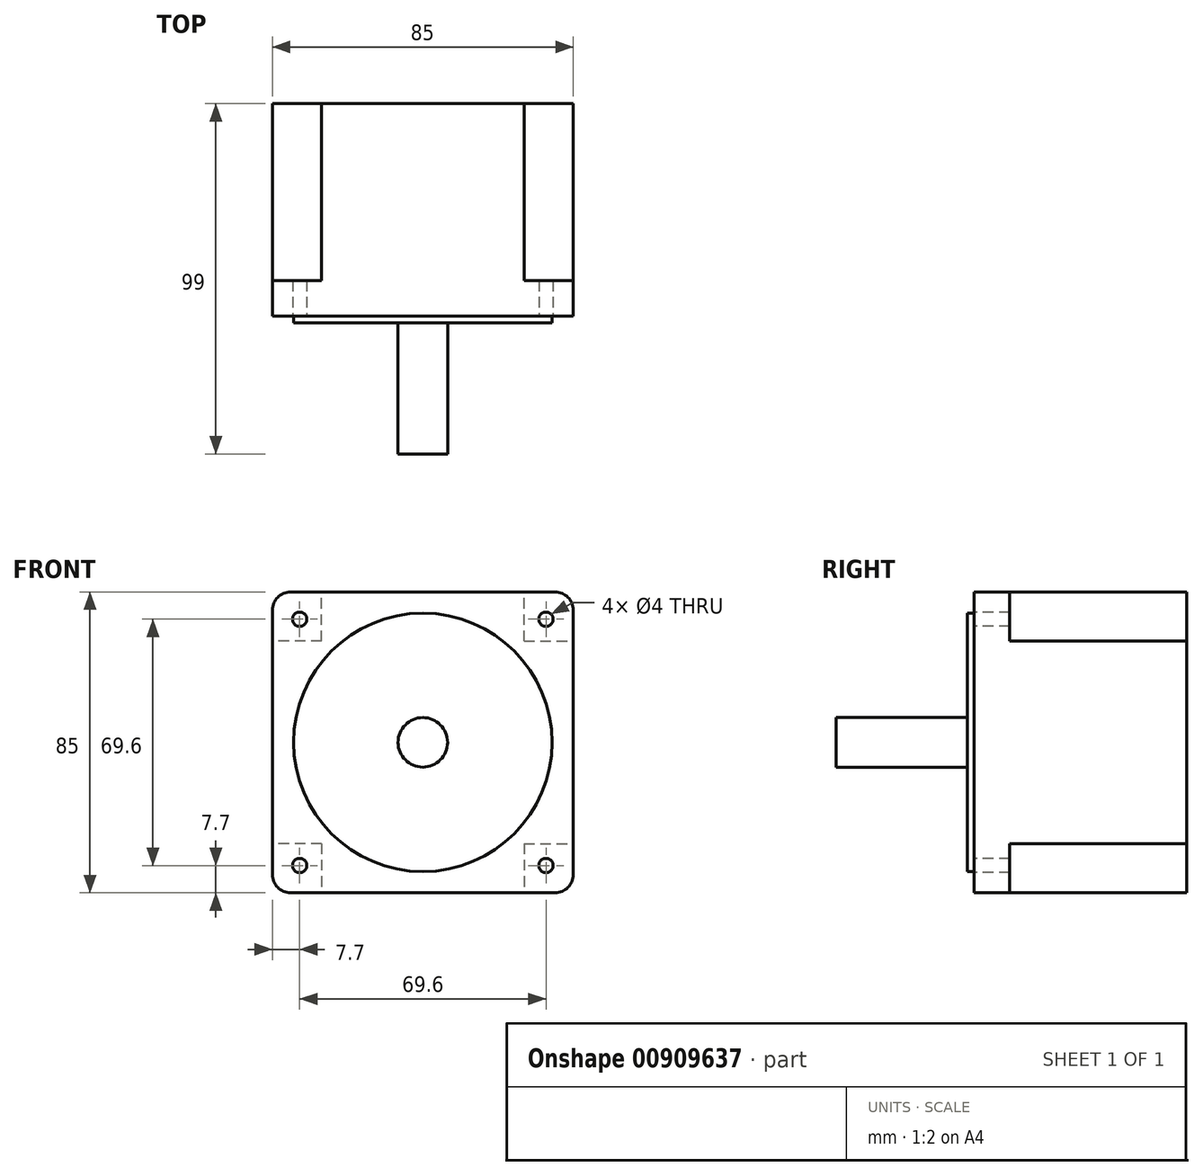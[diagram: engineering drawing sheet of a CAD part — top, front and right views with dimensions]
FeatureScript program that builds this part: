
annotation { "Feature Type Name" : "Feature", "Feature Type Description" : "" }
export const myFeature = defineFeature(function(context is Context, id is Id, definition is map)
    precondition{}
    {
        {
            var Q0;
            Q0=qCreatedBy(makeId("Front.planeOp"),FACE);
            var sketch = newSketch(context, id + "F0", { "sketchPlane" : qUnion([Q0])});
            skLineSegment(sketch, "E0.bottom", {"start": v(42.5, 42.5) * mm, "end": v(-42.5, 42.5) * mm});
            skLineSegment(sketch, "E0.top", {"start": v(42.5, -42.5) * mm, "end": v(-42.5, -42.5) * mm});
            skLineSegment(sketch, "E0.left", {"start": v(42.5, 42.5) * mm, "end": v(42.5, -42.5) * mm});
            skLineSegment(sketch, "E0.right", {"start": v(-42.5, 42.5) * mm, "end": v(-42.5, -42.5) * mm});
            skPoint(sketch, "E0.middle", {"position": v(0, 0) * mm});
            skSolve(sketch);
        }
        {
            var Q0;
            Q0 = qSketchRegion(id + "F0", true);
            extrude(context, id + "F1", {"entities" : qUnion([Q0]), "depth" : 10 * mm, "offsetDistance" : 25.4 * mm});
        }
        {
            var Q0;
            Q0=makeQuery(id+"F1.opExtrude","SWEPT_EDGE",EDGE,{"disambiguationData":[OSD([sQuery(id+"F0.wireOp",EDGE,"E0.top"),sQuery(id+"F0.wireOp",EDGE,"E0.left")])]});
            var Q1;
            Q1=makeQuery(id+"F1.opExtrude","SWEPT_EDGE",EDGE,{"disambiguationData":[OSD([sQuery(id+"F0.wireOp",EDGE,"E0.bottom"),sQuery(id+"F0.wireOp",EDGE,"E0.left")])]});
            var Q2;
            Q2=makeQuery(id+"F1.opExtrude","SWEPT_EDGE",EDGE,{"disambiguationData":[OSD([sQuery(id+"F0.wireOp",EDGE,"E0.bottom"),sQuery(id+"F0.wireOp",EDGE,"E0.right")])]});
            var Q3;
            Q3=makeQuery(id+"F1.opExtrude","SWEPT_EDGE",EDGE,{"disambiguationData":[OSD([sQuery(id+"F0.wireOp",EDGE,"E0.top"),sQuery(id+"F0.wireOp",EDGE,"E0.right")])]});
            fillet(context, id + "F2", {"entities" : qUnion([Q0, Q1, Q2, Q3]), "radius" : 5.08 * mm, "tangentPropagation" : true, "allowEdgeOverflow" : false});
        }
        {
            var Q0;
            Q0=makeQuery(id+"F1.opExtrude","CAP_FACE",FACE,{"disambiguationData":[OSD([sQuery(id+"F0.wireOp",EDGE,"E0.bottom"),sQuery(id+"F0.wireOp",EDGE,"E0.top"),sQuery(id+"F0.wireOp",EDGE,"E0.left"),sQuery(id+"F0.wireOp",EDGE,"E0.right")])],"isStart":false});
            var sketch = newSketch(context, id + "F3", { "sketchPlane" : qUnion([Q0])});
            skPoint(sketch, "E1.middle", {"position": v(0, 0) * mm});
            skCircle(sketch, "E2", {"center": v(-34.8, 34.8) * mm, "radius": 2 * mm});
            skCircle(sketch, "E3", {"center": v(34.8, 34.8) * mm, "radius": 2 * mm});
            skCircle(sketch, "E4", {"center": v(34.8, -34.8) * mm, "radius": 2 * mm});
            skCircle(sketch, "E5", {"center": v(-34.8, -34.8) * mm, "radius": 2 * mm});
            skCircle(sketch, "E6", {"center": v(0, 0) * mm, "radius": 36.51 * mm});
            skSolve(sketch);
        }
        {
            var Q0;
            Q0=makeQuery(id+"F3.imprint","IMPRINT",FACE,{"disambiguationData":[TD([[makeQuery(id+"F3.imprint","IMPRINT",EDGE,{"derivedFrom":sQuery(id+"F3.wireOp",EDGE,"E2")}),1.0]])]});
            var Q1;
            Q1=makeQuery(id+"F3.imprint","IMPRINT",FACE,{"disambiguationData":[TD([[makeQuery(id+"F3.imprint","IMPRINT",EDGE,{"derivedFrom":sQuery(id+"F3.wireOp",EDGE,"E3")}),1.0]])]});
            var Q2;
            Q2=makeQuery(id+"F3.imprint","IMPRINT",FACE,{"disambiguationData":[TD([[makeQuery(id+"F3.imprint","IMPRINT",EDGE,{"derivedFrom":sQuery(id+"F3.wireOp",EDGE,"E4")}),1.0]])]});
            var Q3;
            Q3=makeQuery(id+"F3.imprint","IMPRINT",FACE,{"disambiguationData":[TD([[makeQuery(id+"F3.imprint","IMPRINT",EDGE,{"derivedFrom":sQuery(id+"F3.wireOp",EDGE,"E5")}),1.0]])]});
            extrude(context, id + "F4", {"entities" : qUnion([Q0, Q1, Q2, Q3]), "operationType" : NewBodyOperationType.REMOVE, "oppositeDirection" : true, "depth" : 25.4 * mm, "offsetDistance" : 25.4 * mm});
        }
        {
            var Q0;
            Q0=makeQuery(id+"F3.imprint","IMPRINT",FACE,{"disambiguationData":[TD([[makeQuery(id+"F3.imprint","IMPRINT",EDGE,{"derivedFrom":sQuery(id+"F3.wireOp",EDGE,"E6")}),1.0]])]});
            extrude(context, id + "F5", {"entities" : qUnion([Q0]), "operationType" : NewBodyOperationType.ADD, "depth" : 2 * mm, "offsetDistance" : 25.4 * mm});
        }
        {
            var Q0;
            Q0=makeQuery(id+"F5.opExtrude","CAP_FACE",FACE,{"disambiguationData":[OSD([sQuery(id+"F3.wireOp",EDGE,"E6")])],"isStart":false});
            var sketch = newSketch(context, id + "F6", { "sketchPlane" : qUnion([Q0])});
            skCircle(sketch, "E7", {"center": v(0, 0) * mm, "radius": 7 * mm});
            skSolve(sketch);
        }
        {
            var Q0;
            Q0 = qSketchRegion(id + "F6", true);
            extrude(context, id + "F7", {"entities" : qUnion([Q0]), "operationType" : NewBodyOperationType.ADD, "depth" : 37 * mm, "offsetDistance" : 25.4 * mm});
        }
        {
            var Q0;
            Q0=makeQuery(id+"F1.opExtrude","CAP_FACE",FACE,{"disambiguationData":[OSD([sQuery(id+"F0.wireOp",EDGE,"E0.bottom"),sQuery(id+"F0.wireOp",EDGE,"E0.top"),sQuery(id+"F0.wireOp",EDGE,"E0.left"),sQuery(id+"F0.wireOp",EDGE,"E0.right")])],"isStart":true});
            var sketch = newSketch(context, id + "F8", { "sketchPlane" : qUnion([Q0])});
            skLineSegment(sketch, "E8", {"start": v(34.8, 34.8) * mm, "end": v(41.01, 41.01) * mm, "construction": true});
            skLineSegment(sketch, "E9", {"start": v(41.01, 41.01) * mm, "end": v(28.58, 28.58) * mm, "construction": true});
            skLineSegment(sketch, "E10.bottom", {"start": v(28.58, 28.58) * mm, "end": v(-28.58, 28.58) * mm});
            skLineSegment(sketch, "E10.left", {"start": v(28.58, 28.58) * mm, "end": v(28.58, -28.58) * mm});
            skLineSegment(sketch, "E10.right", {"start": v(-28.58, 28.58) * mm, "end": v(-28.58, -28.58) * mm});
            skPoint(sketch, "E10.middle", {"position": v(0, 0) * mm});
            skLineSegment(sketch, "E11", {"start": v(-28.58, 28.58) * mm, "end": v(-28.58, 42.5) * mm, "construction": true});
            skLineSegment(sketch, "E12", {"start": v(-28.58, -28.58) * mm, "end": v(-42.5, -28.58) * mm, "construction": true});
            skLineSegment(sketch, "E13", {"start": v(-28.58, -28.58) * mm, "end": v(-28.58, -42.5) * mm, "construction": true});
            skLineSegment(sketch, "E14", {"start": v(28.58, -28.58) * mm, "end": v(42.5, -28.58) * mm, "construction": true});
            skLineSegment(sketch, "E15.top", {"start": v(28.58, 42.5) * mm, "end": v(-28.58, 42.5) * mm});
            skLineSegment(sketch, "E15.left", {"start": v(28.58, 28.58) * mm, "end": v(28.58, 42.5) * mm});
            skLineSegment(sketch, "E15.right", {"start": v(-28.58, 28.58) * mm, "end": v(-28.58, 42.5) * mm});
            skLineSegment(sketch, "E16.bottom", {"start": v(-28.58, 28.58) * mm, "end": v(-42.5, 28.58) * mm});
            skLineSegment(sketch, "E16.top", {"start": v(-28.58, -28.58) * mm, "end": v(-42.5, -28.58) * mm});
            skLineSegment(sketch, "E16.right", {"start": v(-42.5, 28.58) * mm, "end": v(-42.5, -28.58) * mm});
            skLineSegment(sketch, "E17.bottom", {"start": v(28.58, -28.58) * mm, "end": v(-28.58, -28.58) * mm});
            skLineSegment(sketch, "E17.top", {"start": v(28.58, -42.5) * mm, "end": v(-28.58, -42.5) * mm});
            skLineSegment(sketch, "E17.left", {"start": v(28.58, -28.58) * mm, "end": v(28.58, -42.5) * mm});
            skLineSegment(sketch, "E17.right", {"start": v(-28.58, -28.58) * mm, "end": v(-28.58, -42.5) * mm});
            skLineSegment(sketch, "E18.bottom", {"start": v(28.58, 28.58) * mm, "end": v(42.5, 28.58) * mm});
            skLineSegment(sketch, "E18.top", {"start": v(28.58, -28.58) * mm, "end": v(42.5, -28.58) * mm});
            skLineSegment(sketch, "E18.right", {"start": v(42.5, 28.58) * mm, "end": v(42.5, -28.58) * mm});
            skSolve(sketch);
        }
        {
            var Q0;
            Q0 = qSketchRegion(id + "F8", true);
            extrude(context, id + "F9", {"entities" : qUnion([Q0]), "operationType" : NewBodyOperationType.ADD, "depth" : 50 * mm, "offsetDistance" : 25.4 * mm});
        }
    });
